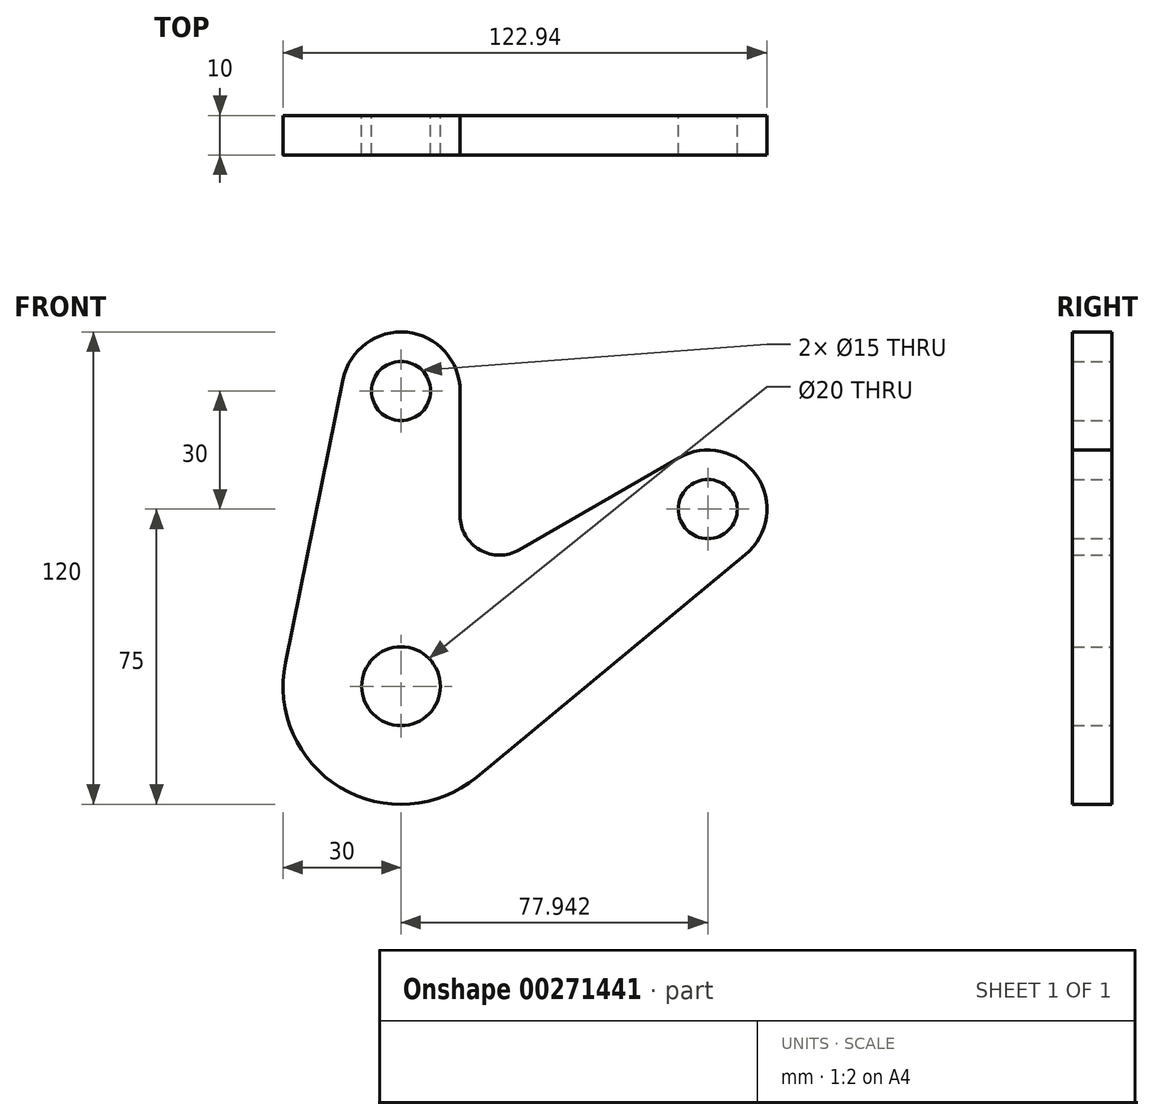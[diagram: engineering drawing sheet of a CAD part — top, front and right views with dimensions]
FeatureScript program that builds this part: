
annotation { "Feature Type Name" : "Feature", "Feature Type Description" : "" }
export const myFeature = defineFeature(function(context is Context, id is Id, definition is map)
    precondition{}
    {
        {
            var Q0;
            Q0=qCreatedBy(makeId("Front.planeOp"),FACE);
            var sketch = newSketch(context, id + "F0", { "sketchPlane" : qUnion([Q0])});
            skCircle(sketch, "E0", {"center": v(0, 0) * mm, "radius": 10 * mm});
            skLineSegment(sketch, "E1", {"start": v(19.12, -23.12) * mm, "end": v(87.5, 33.44) * mm});
            skArc(sketch, "E2", {"start": v(-29.4, 6) * mm, "mid": v(-15.44, -25.72) * mm, "end": v(19.12, -23.12) * mm});
            skCircle(sketch, "E3", {"center": v(0, 75) * mm, "radius": 7.5 * mm});
            skCircle(sketch, "E4", {"center": v(77.94, 45) * mm, "radius": 7.5 * mm});
            skLineSegment(sketch, "E5", {"start": v(-29.4, 6) * mm, "end": v(-14.7, 78) * mm});
            skArc(sketch, "E6", {"start": v(15, 75) * mm, "mid": v(1.5, 89.92) * mm, "end": v(-14.7, 78) * mm});
            skLineSegment(sketch, "E7", {"start": v(15, 75) * mm, "end": v(15, 75) * mm});
            skLineSegment(sketch, "E8", {"start": v(15, 75) * mm, "end": v(15, 43.3) * mm});
            skArc(sketch, "E9", {"start": v(87.5, 33.44) * mm, "mid": v(90.26, 53.56) * mm, "end": v(70.44, 58) * mm});
            skLineSegment(sketch, "E10", {"start": v(70.44, 58) * mm, "end": v(30, 34.64) * mm});
            skArc(sketch, "E11", {"start": v(15, 43.3) * mm, "mid": v(20, 34.64) * mm, "end": v(30, 34.64) * mm});
            skLineSegment(sketch, "E12", {"start": v(0, 0) * mm, "end": v(0, 75) * mm, "construction": true});
            skLineSegment(sketch, "E13", {"start": v(0, 0) * mm, "end": v(77.94, 45) * mm, "construction": true});
            skSolve(sketch);
        }
        {
            var Q0;
            Q0=makeQuery(id+"F0.imprint","IMPRINT",FACE,{"disambiguationData":[TD([[makeQuery(id+"F0.imprint","IMPRINT",EDGE,{"derivedFrom":sQuery(id+"F0.wireOp",EDGE,"E0")}),-1.0]])]});
            extrude(context, id + "F1", {"entities" : qUnion([Q0]), "depth" : 10 * mm});
        }
    });
